# Revit family: Plumbing Fixture_Water Heater_Stiebel Eltron_DHCE
name_source: partatom
category: Plumbing Fixtures
revit_build: Autodesk Revit 2015 (Build: 20140223_1515(x64)
units: mm (PartAtom-declared; Revit-internal decimal feet)

## types (3) — shared parameters
CW Connection = Yes
HW Connection = Yes
Manufacturer = Stiebel Eltron
Manufacturer_Overall Depth = 110 mm  [stored 0.360892 ft]
Manufacturer_Overall Height = 360 mm
Manufacturer_Overall Width = 200 mm  [stored 0.656168 ft]
Manufacturer_URL__Product Specific = http://www.stiebel.com.au
Type Comments = Instantaneous Water Heater
URL = http://www.stiebel.com.au
Vent Connection = No
Waste Connection = No

## per-type parameters (varying)
| type | ApparentLoad_ANZRS | Description | Manufacturer_Spec Code | Model |
| 8/50 | 9600 VA | Instantaneous Single Phase Electric Water Heater - Up to 50°Celsius | DHCE 8/50 | DHCE 8/50 |
| 8/60 | 9600 VA | Instantaneous Single Phase Electric Water Heater - Up to 60°Celsius | DHCE 8/60 | DHCE 8/60 |
| 6/50 | 7200 VA | Instantaneous Single Phase Electric Water Heater - Up to 50°Celsius | DHCE 6/50 | DHCE 6/50 |

note: [stored X ft] marks values corroborated as IEEE doubles in the binary element streams (Revit-internal decimal feet)

## geometry (parser evidence)
native form markers: Sweep x2
no freeform markers — native parametric forms only
